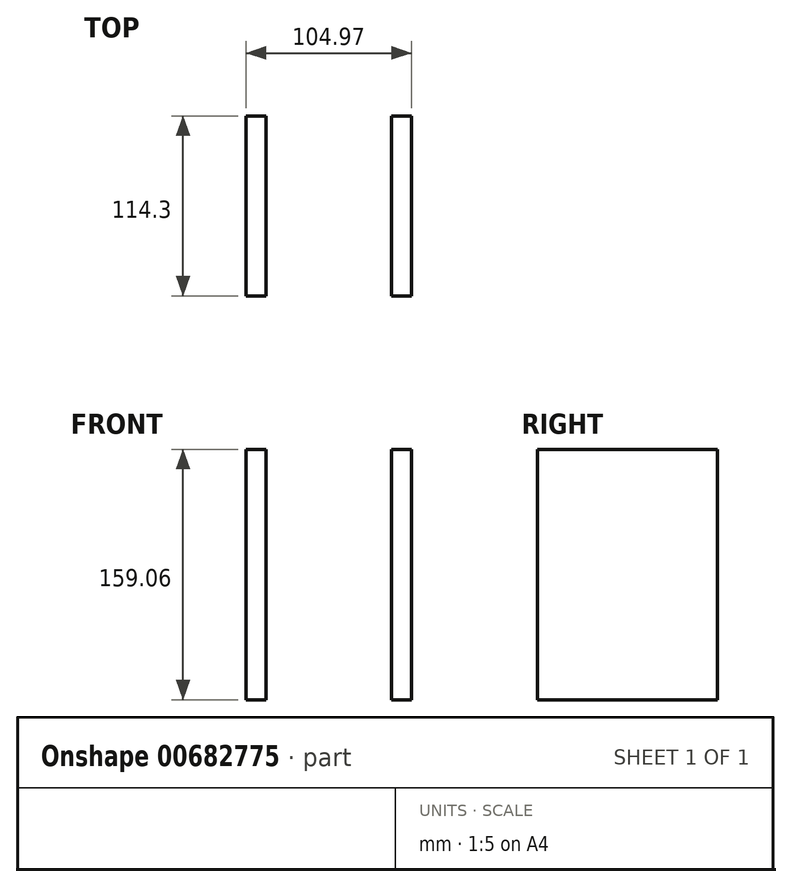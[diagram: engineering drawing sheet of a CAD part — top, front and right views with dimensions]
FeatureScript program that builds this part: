
annotation { "Feature Type Name" : "Feature", "Feature Type Description" : "" }
export const myFeature = defineFeature(function(context is Context, id is Id, definition is map)
    precondition{}
    {
        {
            var Q0;
            Q0=qCreatedBy(makeId("Front.planeOp"),FACE);
            var sketch = newSketch(context, id + "F0", { "sketchPlane" : qUnion([Q0])});
            skLineSegment(sketch, "E0.bottom", {"start": v(-47.89, -79.53) * mm, "end": v(-35.32, -79.53) * mm});
            skLineSegment(sketch, "E0.top", {"start": v(-47.89, 79.53) * mm, "end": v(-35.32, 79.53) * mm});
            skLineSegment(sketch, "E0.left", {"start": v(-47.89, -79.53) * mm, "end": v(-47.89, 79.53) * mm});
            skLineSegment(sketch, "E0.right", {"start": v(-35.32, -79.53) * mm, "end": v(-35.32, 79.53) * mm});
            skSolve(sketch);
        }
        {
            var Q0;
            Q0=makeQuery(id+"F0.imprint","IMPRINT",FACE,{"disambiguationData":[TD([[makeQuery(id+"F0.imprint","IMPRINT",EDGE,{"derivedFrom":sQuery(id+"F0.wireOp",EDGE,"E0.bottom")}),1.0]])]});
            extrude(context, id + "F1", {"entities" : qUnion([Q0]), "depth" : 57.15 * mm, "offsetDistance" : 25.4 * mm, "hasSecondDirection" : true, "secondDirectionOppositeDirection" : true, "secondDirectionDepth" : 57.15 * mm});
        }
        {
            var Q0;
            Q0=qCreatedBy(makeId("Front.planeOp"),FACE);
            var sketch = newSketch(context, id + "F2", { "sketchPlane" : qUnion([Q0])});
            skLineSegment(sketch, "E1.bottom", {"start": v(-6.28, -79.53) * mm, "end": v(6.28, -79.53) * mm});
            skLineSegment(sketch, "E1.top", {"start": v(-6.28, 79.53) * mm, "end": v(6.28, 79.53) * mm});
            skLineSegment(sketch, "E1.left", {"start": v(-6.28, -79.53) * mm, "end": v(-6.28, 79.53) * mm});
            skLineSegment(sketch, "E1.right", {"start": v(6.28, -79.53) * mm, "end": v(6.28, 79.53) * mm});
            skSolve(sketch);
        }
        {
            var Q0;
            Q0=makeQuery(id+"F2.imprint","IMPRINT",FACE,{"disambiguationData":[TD([[makeQuery(id+"F2.imprint","IMPRINT",EDGE,{"derivedFrom":sQuery(id+"F2.wireOp",EDGE,"E1.bottom")}),1.0]])]});
            extrude(context, id + "F3", {"entities" : qUnion([Q0]), "depth" : 57.15 * mm, "offsetDistance" : 25.4 * mm, "hasSecondDirection" : true, "secondDirectionOppositeDirection" : true, "secondDirectionDepth" : 57.15 * mm});
        }
        {
            var Q0;
            Q0=makeQuery(id+"F3.opExtrude","SWEPT_BODY",BODY,{"disambiguationData":[OSD([sQuery(id+"F2.wireOp",EDGE,"E1.bottom"),sQuery(id+"F2.wireOp",EDGE,"E1.top"),sQuery(id+"F2.wireOp",EDGE,"E1.left"),sQuery(id+"F2.wireOp",EDGE,"E1.right")])]});
            var Q1;
            Q1=qCreatedBy(makeId("Right.planeOp"),FACE);
            transform(context, id + "F4", {"entities" : qUnion([Q0]), "transformType" : TransformType.TRANSLATION_DISTANCE, "transformDirection" : qUnion([Q1]), "distance" : 50.8 * mm, "makeCopy" : false});
        }
    });
